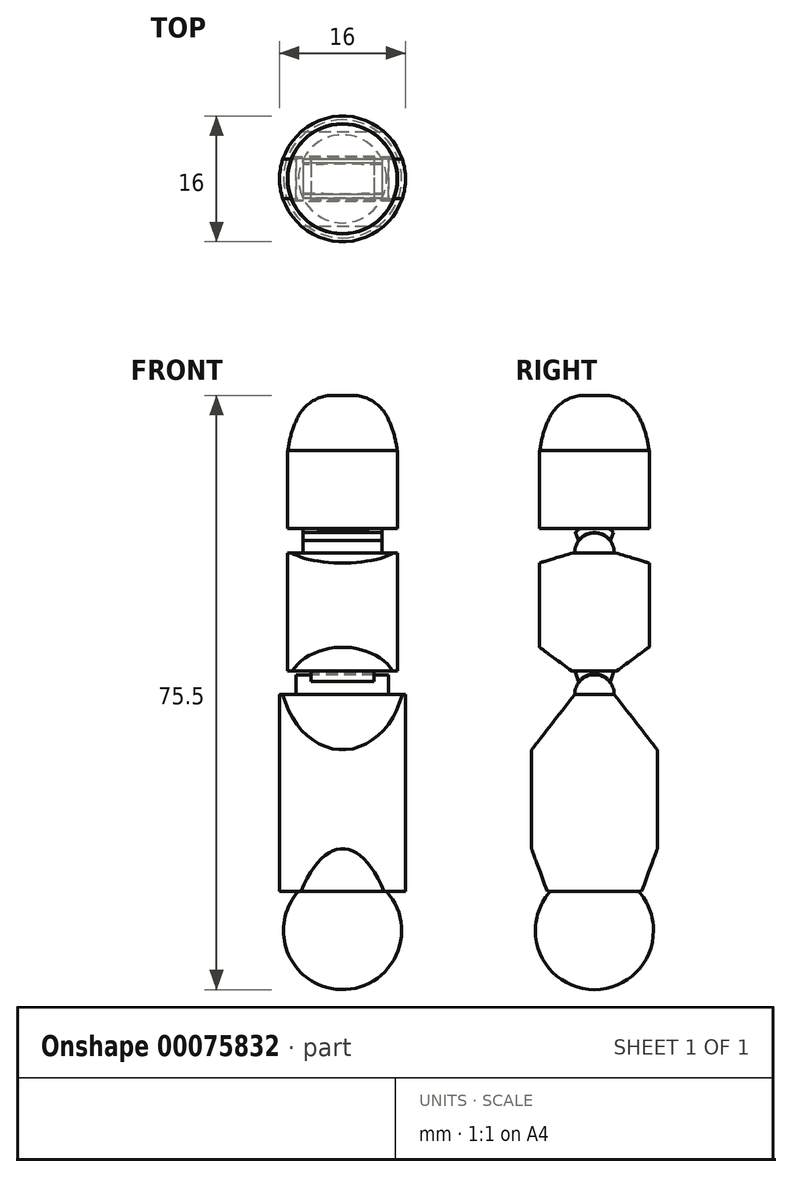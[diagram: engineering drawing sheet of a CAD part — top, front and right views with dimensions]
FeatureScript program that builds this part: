
annotation { "Feature Type Name" : "Feature", "Feature Type Description" : "" }
export const myFeature = defineFeature(function(context is Context, id is Id, definition is map)
    precondition{}
    {
        {
            var Q0;
            Q0=qCreatedBy(makeId("Top.planeOp"),FACE);
            var sketch = newSketch(context, id + "F0", { "sketchPlane" : qUnion([Q0])});
            skArc(sketch, "E0", {"start": v(0, 7.5) * mm, "mid": v(-7.5, 0) * mm, "end": v(0, -7.5) * mm});
            skLineSegment(sketch, "E1", {"start": v(0, 7.5) * mm, "end": v(0, -7.5) * mm});
            skSolve(sketch);
        }
        {
            var Q0;
            Q0 = qSketchRegion(id + "F0", true);
            var Q1;
            Q1=sQuery(id+"F0.wireOp",EDGE,"E1");
            revolve(context, id + "F1", {"entities" : qUnion([Q0]), "axis" : qUnion([Q1]), "revolveType" : RevolveType.FULL});
        }
        {
            var Q0;
            Q0=qCreatedBy(makeId("Top.planeOp"),FACE);
            cPlane(context, id + "F2", {"entities" : qUnion([Q0]), "cplaneType" : CPlaneType.OFFSET, "offset" : 5 * mm, "width" : 150 * mm, "height" : 150 * mm});
        }
        {
            var Q0;
            Q0=qCreatedBy(id+"F2.planeOp",FACE);
            var sketch = newSketch(context, id + "F3", { "sketchPlane" : qUnion([Q0])});
            skCircle(sketch, "E2", {"center": v(0, 0) * mm, "radius": 8 * mm});
            skSolve(sketch);
        }
        {
            var Q0;
            Q0 = qSketchRegion(id + "F3", true);
            extrude(context, id + "F4", {"entities" : qUnion([Q0]), "operationType" : NewBodyOperationType.ADD, "depth" : 25 * mm});
        }
        {
            var Q0;
            Q0=qCreatedBy(makeId("Right.planeOp"),FACE);
            var sketch = newSketch(context, id + "F5", { "sketchPlane" : qUnion([Q0])});
            skCircle(sketch, "E3", {"center": v(0, 30) * mm, "radius": 2.5 * mm});
            skSolve(sketch);
        }
        {
            var Q0;
            Q0=makeQuery(id+"F5.imprint","IMPRINT",FACE,{"disambiguationData":[TD([[makeQuery(id+"F5.imprint","IMPRINT",EDGE,{"derivedFrom":sQuery(id+"F5.wireOp",EDGE,"E3")}),1.0]])]});
            var Q1;
            Q1=sQuery(id+"F5.wireOp",EDGE,"E3");
            extrude(context, id + "F6", {"entities" : qUnion([Q0]), "operationType" : NewBodyOperationType.ADD, "surfaceEntities" : qUnion([Q1]), "depth" : 5.85 * mm, "hasSecondDirection" : true, "secondDirectionOppositeDirection" : true, "secondDirectionDepth" : 5.9 * mm});
        }
        {
            var Q0;
            Q0=qCreatedBy(makeId("Right.planeOp"),FACE);
            var sketch = newSketch(context, id + "F7", { "sketchPlane" : qUnion([Q0])});
            skLineSegment(sketch, "E4", {"start": v(2.5, 30) * mm, "end": v(10.5, 19.75) * mm});
            skLineSegment(sketch, "E5", {"start": v(10.5, 19.75) * mm, "end": v(10.5, 30) * mm});
            skLineSegment(sketch, "E6", {"start": v(10.5, 30) * mm, "end": v(2.5, 30) * mm});
            skLineSegment(sketch, "E7", {"start": v(-2.5, 30) * mm, "end": v(-10.5, 30) * mm});
            skLineSegment(sketch, "E8", {"start": v(-10.5, 30) * mm, "end": v(-10.5, 19.75) * mm});
            skLineSegment(sketch, "E9", {"start": v(-10.5, 19.75) * mm, "end": v(-2.5, 30) * mm});
            skLineSegment(sketch, "E10", {"start": v(-10.5, 5) * mm, "end": v(-6, 5) * mm});
            skLineSegment(sketch, "E11", {"start": v(-6, 5) * mm, "end": v(-10.5, 17.2) * mm});
            skLineSegment(sketch, "E12", {"start": v(-10.5, 17.2) * mm, "end": v(-10.5, 5) * mm});
            skLineSegment(sketch, "E13", {"start": v(6, 5) * mm, "end": v(10.5, 5) * mm});
            skLineSegment(sketch, "E14", {"start": v(10.5, 5) * mm, "end": v(10.5, 17.2) * mm});
            skLineSegment(sketch, "E15", {"start": v(10.5, 17.2) * mm, "end": v(6, 5) * mm});
            skSolve(sketch);
        }
        {
            var Q0;
            Q0 = qSketchRegion(id + "F7", true);
            extrude(context, id + "F8", {"entities" : qUnion([Q0]), "operationType" : NewBodyOperationType.REMOVE, "oppositeDirection" : true, "depth" : 25 * mm, "hasSecondDirection" : true, "secondDirectionOppositeDirection" : false, "secondDirectionDepth" : 25 * mm});
        }
        {
            var Q0;
            Q0=qCreatedBy(makeId("Right.planeOp"),FACE);
            var sketch = newSketch(context, id + "F9", { "sketchPlane" : qUnion([Q0])});
            skArc(sketch, "E16", {"start": v(2.6, 30) * mm, "mid": v(0, 32.6) * mm, "end": v(-2.6, 30) * mm});
            skLineSegment(sketch, "E17", {"start": v(-2.6, 30) * mm, "end": v(-4, 30) * mm});
            skLineSegment(sketch, "E18", {"start": v(2.6, 30) * mm, "end": v(4, 30) * mm});
            skArc(sketch, "E19", {"start": v(4, 30) * mm, "mid": v(0, 34) * mm, "end": v(-4, 30) * mm});
            skLineSegment(sketch, "E20", {"start": v(0, 32.6) * mm, "end": v(0, 34) * mm, "construction": true});
            skSolve(sketch);
        }
        {
            var Q0;
            Q0 = qSketchRegion(id + "F9", true);
            extrude(context, id + "F10", {"entities" : qUnion([Q0]), "depth" : 4 * mm, "hasSecondDirection" : true, "secondDirectionOppositeDirection" : true, "secondDirectionDepth" : 4 * mm});
        }
        {
            var Q0;
            Q0=qCreatedBy(makeId("Right.planeOp"),FACE);
            var sketch = newSketch(context, id + "F11", { "sketchPlane" : qUnion([Q0])});
            skLineSegment(sketch, "E21", {"start": v(0, 33) * mm, "end": v(0, 48) * mm});
            skLineSegment(sketch, "E22", {"start": v(0, 48) * mm, "end": v(-7, 48) * mm});
            skLineSegment(sketch, "E23", {"start": v(-7, 48) * mm, "end": v(-7, 32.97) * mm});
            skLineSegment(sketch, "E24", {"start": v(-7, 32.97) * mm, "end": v(0, 33) * mm});
            skSolve(sketch);
        }
        {
            var Q0;
            Q0=makeQuery(id+"F11.imprint","IMPRINT",FACE,{"disambiguationData":[TD([[makeQuery(id+"F11.imprint","IMPRINT",EDGE,{"derivedFrom":sQuery(id+"F11.wireOp",EDGE,"E21")}),1.0]])]});
            var Q1;
            Q1=sQuery(id+"F11.wireOp",EDGE,"E21");
            revolve(context, id + "F12", {"operationType" : NewBodyOperationType.ADD, "entities" : qUnion([Q0]), "axis" : qUnion([Q1]), "revolveType" : RevolveType.FULL});
        }
        {
            var Q0;
            Q0=makeQuery(id+"F10.opExtrude","SWEPT_EDGE",EDGE,{"disambiguationData":[OSD([sQuery(id+"F9.wireOp",EDGE,"E17"),sQuery(id+"F9.wireOp",EDGE,"E19")])]});
            var Q1;
            Q1=makeQuery(id+"F10.opExtrude","SWEPT_EDGE",EDGE,{"disambiguationData":[OSD([sQuery(id+"F9.wireOp",EDGE,"E18"),sQuery(id+"F9.wireOp",EDGE,"E19")])]});
            chamfer(context, id + "F13", {"entities" : qUnion([Q0, Q1]), "width" : 1.75 * mm, "tangentPropagation" : true});
        }
        {
            var Q0;
            Q0=qCreatedBy(makeId("Right.planeOp"),FACE);
            var sketch = newSketch(context, id + "F14", { "sketchPlane" : qUnion([Q0])});
            skArc(sketch, "E25", {"start": v(2.5, 48) * mm, "mid": v(0, 50.5) * mm, "end": v(-2.5, 48) * mm});
            skLineSegment(sketch, "E26", {"start": v(2.5, 48) * mm, "end": v(-2.5, 48) * mm});
            skPoint(sketch, "E27", {"position": v(2.5, 48) * mm});
            skSolve(sketch);
        }
        {
            var Q0;
            Q0 = qSketchRegion(id + "F14", true);
            extrude(context, id + "F15", {"entities" : qUnion([Q0]), "operationType" : NewBodyOperationType.ADD, "depth" : 5 * mm, "hasSecondDirection" : true, "secondDirectionOppositeDirection" : true, "secondDirectionDepth" : 5 * mm});
        }
        {
            var Q0;
            Q0=qCreatedBy(makeId("Right.planeOp"),FACE);
            var sketch = newSketch(context, id + "F16", { "sketchPlane" : qUnion([Q0])});
            skLineSegment(sketch, "E28", {"start": v(-2.85, 32.97) * mm, "end": v(-7.13, 36.1) * mm});
            skLineSegment(sketch, "E29", {"start": v(-7.13, 36.1) * mm, "end": v(-7.13, 32.97) * mm});
            skLineSegment(sketch, "E30", {"start": v(-7.13, 32.97) * mm, "end": v(-2.85, 32.97) * mm});
            skLineSegment(sketch, "E31", {"start": v(2.79, 32.97) * mm, "end": v(7.07, 36.1) * mm});
            skLineSegment(sketch, "E32", {"start": v(7.07, 36.1) * mm, "end": v(7.07, 32.97) * mm});
            skLineSegment(sketch, "E33", {"start": v(7.07, 32.97) * mm, "end": v(2.79, 32.97) * mm});
            skLineSegment(sketch, "E34", {"start": v(-2.73, 48) * mm, "end": v(-7.13, 48) * mm});
            skLineSegment(sketch, "E35", {"start": v(-7.13, 48) * mm, "end": v(-7.13, 46.66) * mm});
            skLineSegment(sketch, "E36", {"start": v(-7.13, 46.66) * mm, "end": v(-2.73, 48) * mm});
            skLineSegment(sketch, "E37", {"start": v(2.66, 48) * mm, "end": v(7.07, 48) * mm});
            skLineSegment(sketch, "E38", {"start": v(7.07, 48) * mm, "end": v(7.07, 46.66) * mm});
            skLineSegment(sketch, "E39", {"start": v(7.07, 46.66) * mm, "end": v(2.66, 48) * mm});
            skSolve(sketch);
        }
        {
            var Q0;
            Q0 = qSketchRegion(id + "F16", true);
            extrude(context, id + "F17", {"entities" : qUnion([Q0]), "operationType" : NewBodyOperationType.REMOVE, "oppositeDirection" : true, "depth" : 25 * mm, "hasSecondDirection" : true, "secondDirectionOppositeDirection" : false, "secondDirectionDepth" : 25 * mm});
        }
        {
            var Q0;
            Q0=qCreatedBy(makeId("Right.planeOp"),FACE);
            var sketch = newSketch(context, id + "F18", { "sketchPlane" : qUnion([Q0])});
            skArc(sketch, "E40", {"start": v(2.55, 48) * mm, "mid": v(0, 50.55) * mm, "end": v(-2.55, 48) * mm});
            skPoint(sketch, "E41", {"position": v(-2.55, 48) * mm});
            skLineSegment(sketch, "E42", {"start": v(-2.55, 48) * mm, "end": v(-3.55, 48) * mm});
            skLineSegment(sketch, "E43", {"start": v(2.55, 48) * mm, "end": v(3.55, 48) * mm});
            skLineSegment(sketch, "E44", {"start": v(0, 50.55) * mm, "end": v(0, 51.55) * mm, "construction": true});
            skPoint(sketch, "E44.endSnap0", {"position": v(0, 50.55) * mm});
            skArc(sketch, "E45", {"start": v(3.55, 48) * mm, "mid": v(0, 51.55) * mm, "end": v(-3.55, 48) * mm});
            skSolve(sketch);
        }
        {
            var Q0;
            Q0 = qSketchRegion(id + "F18", true);
            extrude(context, id + "F19", {"entities" : qUnion([Q0]), "depth" : 5 * mm, "hasSecondDirection" : true, "secondDirectionOppositeDirection" : true, "secondDirectionDepth" : 5 * mm});
        }
        {
            var Q0;
            Q0=qCreatedBy(makeId("Right.planeOp"),FACE);
            var sketch = newSketch(context, id + "F20", { "sketchPlane" : qUnion([Q0])});
            skLineSegment(sketch, "E46", {"start": v(0, 51) * mm, "end": v(0, 61) * mm});
            skLineSegment(sketch, "E47", {"start": v(0, 61) * mm, "end": v(-7, 61) * mm});
            skLineSegment(sketch, "E48", {"start": v(-7, 61) * mm, "end": v(-7, 51.1) * mm});
            skLineSegment(sketch, "E49", {"start": v(-7, 51.1) * mm, "end": v(0, 51) * mm});
            skSolve(sketch);
        }
        {
            var Q0;
            Q0=makeQuery(id+"F20.imprint","IMPRINT",FACE,{"disambiguationData":[TD([[makeQuery(id+"F20.imprint","IMPRINT",EDGE,{"derivedFrom":sQuery(id+"F20.wireOp",EDGE,"E46")}),1.0]])]});
            var Q1;
            Q1=sQuery(id+"F20.wireOp",EDGE,"E46");
            revolve(context, id + "F21", {"operationType" : NewBodyOperationType.ADD, "entities" : qUnion([Q0]), "axis" : qUnion([Q1]), "revolveType" : RevolveType.FULL});
        }
        {
            var Q0;
            Q0=qCreatedBy(makeId("Right.planeOp"),FACE);
            var sketch = newSketch(context, id + "F22", { "sketchPlane" : qUnion([Q0])});
            skLineSegment(sketch, "E50", {"start": v(0, 61) * mm, "end": v(0, 71) * mm});
            skArc(sketch, "E51", {"start": v(0, 71) * mm, "mid": v(-4.71, 66.86) * mm, "end": v(-6.94, 61) * mm});
            skLineSegment(sketch, "E52", {"start": v(0, 61) * mm, "end": v(-6.94, 61) * mm});
            skSolve(sketch);
        }
        {
            var Q0;
            Q0=makeQuery(id+"F22.imprint","IMPRINT",FACE,{"disambiguationData":[TD([[makeQuery(id+"F22.imprint","IMPRINT",EDGE,{"derivedFrom":sQuery(id+"F22.wireOp",EDGE,"E50")}),1.0]])]});
            var Q1;
            Q1=sQuery(id+"F22.wireOp",EDGE,"E50");
            revolve(context, id + "F23", {"operationType" : NewBodyOperationType.ADD, "entities" : qUnion([Q0]), "axis" : qUnion([Q1]), "revolveType" : RevolveType.FULL});
        }
        {
            var Q0;
            Q0=qCreatedBy(makeId("Right.planeOp"),FACE);
            var sketch = newSketch(context, id + "F24", { "sketchPlane" : qUnion([Q0])});
            skLineSegment(sketch, "E53.bottom", {"start": v(-5, 71) * mm, "end": v(5, 71) * mm});
            skLineSegment(sketch, "E53.top", {"start": v(-5, 68) * mm, "end": v(5, 68) * mm});
            skLineSegment(sketch, "E53.left", {"start": v(-5, 71) * mm, "end": v(-5, 68) * mm});
            skLineSegment(sketch, "E53.right", {"start": v(5, 71) * mm, "end": v(5, 68) * mm});
            skPoint(sketch, "E54", {"position": v(0, 71) * mm});
            skSolve(sketch);
        }
        {
            var Q0;
            Q0 = qSketchRegion(id + "F24", true);
            extrude(context, id + "F25", {"entities" : qUnion([Q0]), "operationType" : NewBodyOperationType.REMOVE, "oppositeDirection" : true, "depth" : 25 * mm, "hasSecondDirection" : true, "secondDirectionOppositeDirection" : false, "secondDirectionDepth" : 25 * mm});
        }
        {
            var Q0;
            Q0=makeQuery(id+"F25.boolean.opBoolean","INTERSECT",EDGE,{"derivedFrom":[makeQuery(id+"F23.opRevolve","SWEPT_FACE",FACE,{"disambiguationData":[OSD([sQuery(id+"F22.wireOp",EDGE,"E51")])]}),makeQuery(id+"F25.opExtrude","SWEPT_FACE",FACE,{"disambiguationData":[OSD([sQuery(id+"F24.wireOp",EDGE,"E53.top")])]})]});
            fillet(context, id + "F26", {"entities" : qUnion([Q0]), "radius" : 5 * mm, "tangentPropagation" : true, "allowEdgeOverflow" : false});
        }
        {
            var Q0;
            Q0=makeQuery(id+"F19.opExtrude","SWEPT_EDGE",EDGE,{"disambiguationData":[OSD([sQuery(id+"F18.wireOp",EDGE,"E42"),sQuery(id+"F18.wireOp",EDGE,"E45")])]});
            var Q1;
            Q1=makeQuery(id+"F19.opExtrude","SWEPT_EDGE",EDGE,{"disambiguationData":[OSD([sQuery(id+"F18.wireOp",EDGE,"E43"),sQuery(id+"F18.wireOp",EDGE,"E45")])]});
            chamfer(context, id + "F27", {"entities" : qUnion([Q0, Q1]), "width" : 1.5 * mm, "tangentPropagation" : true});
        }
    });
